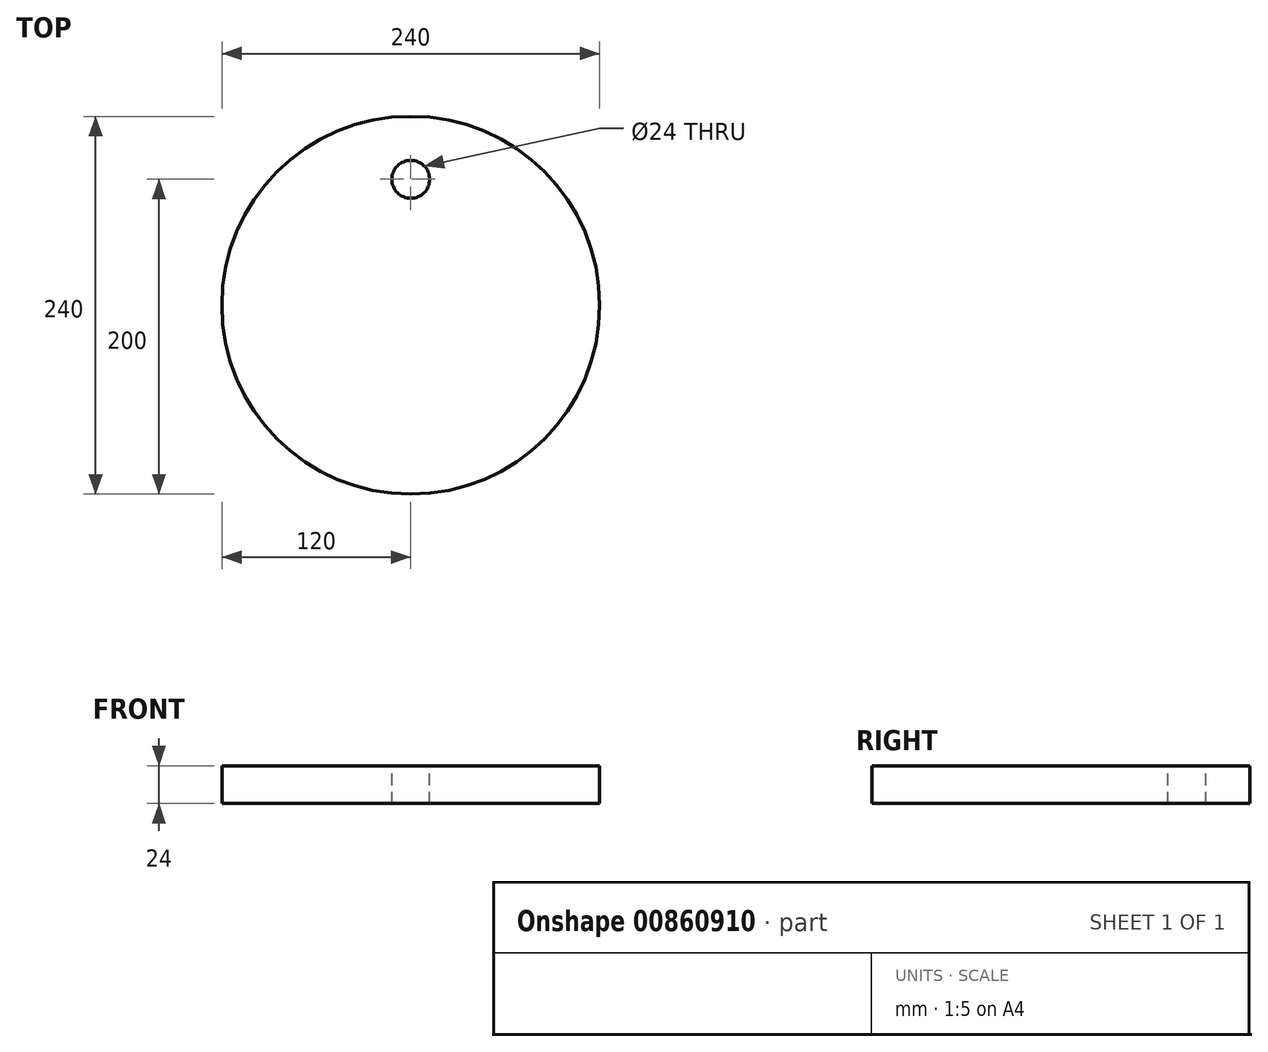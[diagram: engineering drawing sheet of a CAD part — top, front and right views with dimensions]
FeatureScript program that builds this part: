
annotation { "Feature Type Name" : "Feature", "Feature Type Description" : "" }
export const myFeature = defineFeature(function(context is Context, id is Id, definition is map)
    precondition{}
    {
        {
            assignVariable(context, id + "F0", {"name" : "big_circle", "anyValue" : 240});
        }
        {
            assignVariable(context, id + "F1", {"name" : "thickness", "anyValue" : getVariable(context, 'big_circle') / 10});
        }
        {
            var Q0;
            Q0=qCreatedBy(makeId("Top.planeOp"),FACE);
            var sketch = newSketch(context, id + "F2", { "sketchPlane" : qUnion([Q0])});
            skCircle(sketch, "E0", {"center": v(0, 0) * mm, "radius": 120 * mm});
            skSolve(sketch);
        }
        {
            var Q0;
            Q0=qSketchRegion(id+"F2",true);
            extrude(context, id + "F3", {"entities" : qUnion([Q0]), "depth" : (getVariable(context, 'thickness')) * mm, "offsetDistance" : 25 * mm});
        }
        {
            var Q0;
            Q0=makeQuery(id+"F3.opExtrude","CAP_FACE",FACE,{"disambiguationData":[OSD([sQuery(id+"F2.wireOp",EDGE,"E0")])],"isStart":false});
            var sketch = newSketch(context, id + "F4", { "sketchPlane" : qUnion([Q0])});
            skCircle(sketch, "E1", {"center": v(0, 0) * mm, "radius": 80 * mm, "construction": true});
            skCircle(sketch, "E2", {"center": v(0, 80) * mm, "radius": 12 * mm});
            skSolve(sketch);
        }
        {
            var Q0;
            Q0=makeQuery(id+"F4.imprint","IMPRINT",FACE,{"disambiguationData":[TD([[makeQuery(id+"F4.imprint","IMPRINT",EDGE,{"derivedFrom":sQuery(id+"F4.wireOp",EDGE,"E2")}),1.0]])]});
            extrude(context, id + "F5", {"entities" : qUnion([Q0]), "operationType" : NewBodyOperationType.REMOVE, "endBound" : BoundingType.THROUGH_ALL, "oppositeDirection" : true, "depth" : 25 * mm, "offsetDistance" : 25 * mm});
        }
    });
